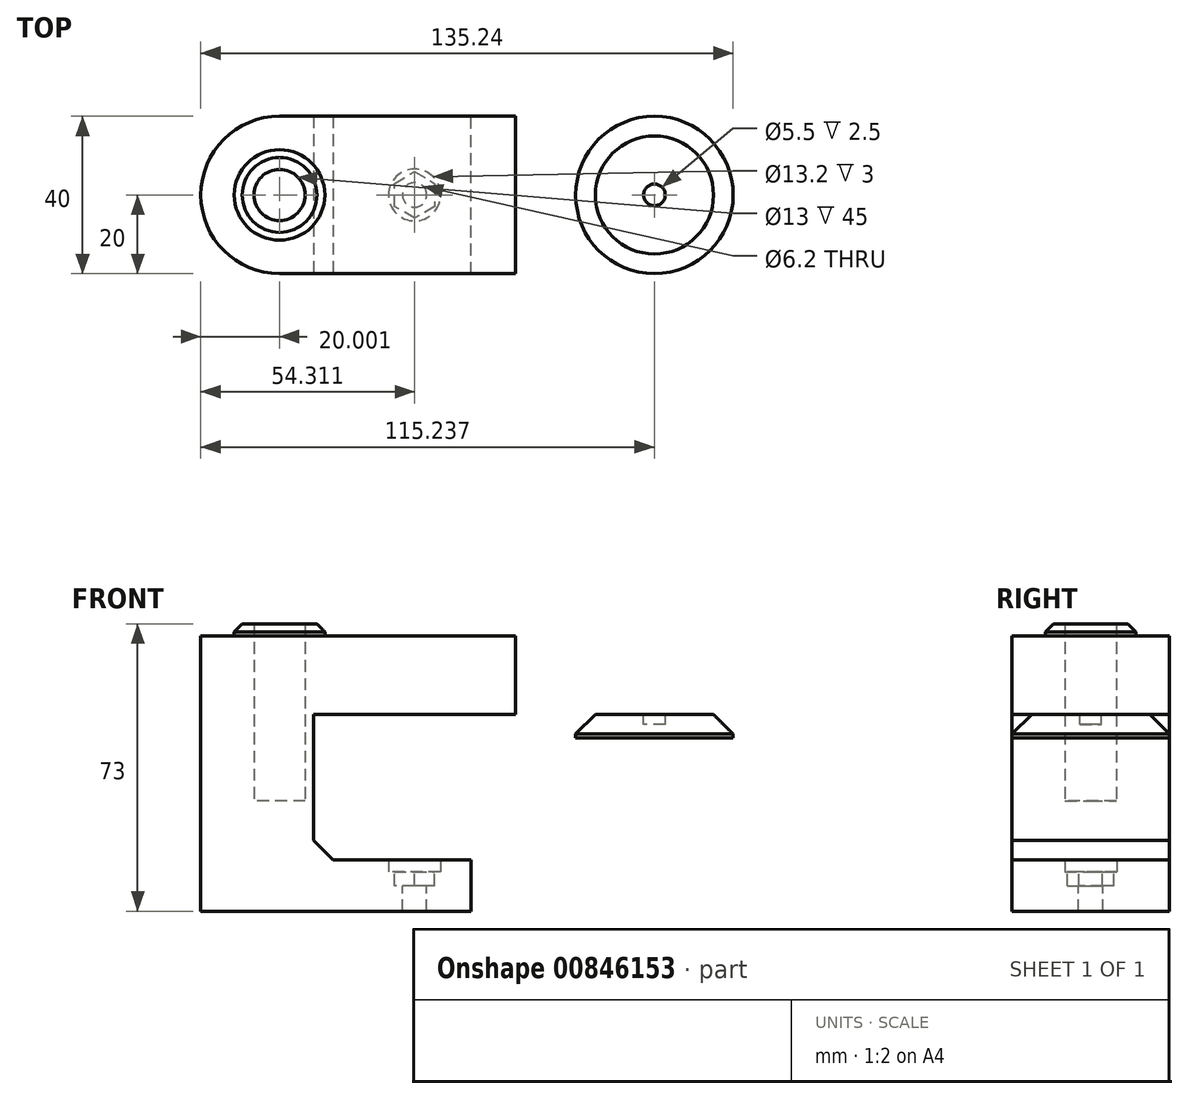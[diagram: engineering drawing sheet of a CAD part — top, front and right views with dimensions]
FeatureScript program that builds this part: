
annotation { "Feature Type Name" : "Feature", "Feature Type Description" : "" }
export const myFeature = defineFeature(function(context is Context, id is Id, definition is map)
    precondition{}
    {
        {
            var Q0;
            Q0=qCreatedBy(makeId("Top.planeOp"),FACE);
            var sketch = newSketch(context, id + "F0", { "sketchPlane" : qUnion([Q0])});
            skCircle(sketch, "E0", {"center": v(-23.62, 0) * mm, "radius": 6.5 * mm});
            skLineSegment(sketch, "E1", {"start": v(-23.62, 20) * mm, "end": v(36.38, 20) * mm});
            skLineSegment(sketch, "E2", {"start": v(36.38, 20) * mm, "end": v(36.38, -20) * mm});
            skLineSegment(sketch, "E3", {"start": v(36.38, -20) * mm, "end": v(-23.62, -20) * mm});
            skLineSegment(sketch, "E4", {"start": v(-69.54, 0) * mm, "end": v(66.59, 0) * mm, "construction": true});
            skLineSegment(sketch, "E5", {"start": v(-23.62, 57.59) * mm, "end": v(-23.62, -47.6) * mm, "construction": true});
            skPoint(sketch, "E6", {"position": v(36.38, 0) * mm});
            skCircle(sketch, "E7", {"center": v(-23.62, 0) * mm, "radius": 20 * mm});
            skPoint(sketch, "E8", {"position": v(-43.62, 0) * mm});
            skPoint(sketch, "E9", {"position": v(-23.62, 20) * mm});
            skPoint(sketch, "E10", {"position": v(-23.62, -20) * mm});
            skSolve(sketch);
        }
        {
            var Q0;
            {var subQ0=sQuery(id+"F0.wireOp",EDGE,"E1");Q0=makeQuery(id+"F0.imprint","IMPRINT",FACE,{"disambiguationData":[TD([[makeQuery(id+"F0.imprint","IMPRINT",EDGE,{"derivedFrom":subQ0}),-1.0]])]});}
            var Q1;
            Q1=makeQuery(id+"F0.imprint","IMPRINT",FACE,{"disambiguationData":[TD([[makeQuery(id+"F0.imprint","IMPRINT",EDGE,{"derivedFrom":sQuery(id+"F0.wireOp",EDGE,"E0")}),-1.0]])]});
            extrude(context, id + "F1", {"entities" : qUnion([Q0, Q1]), "depth" : 20 * mm, "offsetDistance" : 25 * mm});
        }
        {
            var Q0;
            Q0=qCreatedBy(makeId("Top.planeOp"),FACE);
            var sketch = newSketch(context, id + "F2", { "sketchPlane" : qUnion([Q0])});
            skLineSegment(sketch, "E11", {"start": v(-15, 20) * mm, "end": v(-15, -20) * mm});
            skPoint(sketch, "E12", {"position": v(-15, 0) * mm});
            skLineSegment(sketch, "E13", {"start": v(-15, 20) * mm, "end": v(-23.62, 20) * mm});
            skLineSegment(sketch, "E14.MirrorCS", {"start": v(-15, -20) * mm, "end": v(-23.62, -20) * mm});
            skArc(sketch, "E15", {"start": v(-23.62, 20) * mm, "mid": v(-43.62, 0) * mm, "end": v(-23.62, -20) * mm});
            skSolve(sketch);
        }
        {
            var Q0;
            Q0 = qSketchRegion(id + "F2", true);
            extrude(context, id + "F3", {"entities" : qUnion([Q0]), "operationType" : NewBodyOperationType.ADD, "oppositeDirection" : true, "depth" : 50 * mm, "offsetDistance" : 25 * mm});
        }
        {
            var Q0;
            Q0=makeQuery(id+"F0.imprint","IMPRINT",FACE,{"disambiguationData":[TD([[makeQuery(id+"F0.imprint","IMPRINT",EDGE,{"derivedFrom":sQuery(id+"F0.wireOp",EDGE,"E0")}),1.0]])]});
            extrude(context, id + "F4", {"entities" : qUnion([Q0]), "operationType" : NewBodyOperationType.REMOVE, "oppositeDirection" : true, "depth" : 22 * mm, "offsetDistance" : 25 * mm});
        }
        {
            var Q0;
            Q0=makeQuery(id+"F3.opExtrude","CAP_FACE",FACE,{"disambiguationData":[OSD([sQuery(id+"F2.wireOp",EDGE,"E11"),sQuery(id+"F2.wireOp",EDGE,"E13"),sQuery(id+"F2.wireOp",EDGE,"E14.MirrorCS"),sQuery(id+"F2.wireOp",EDGE,"E15")])],"isStart":false});
            var sketch = newSketch(context, id + "F5", { "sketchPlane" : qUnion([Q0])});
            skLineSegment(sketch, "E16.bottom", {"start": v(25, 20) * mm, "end": v(-15, 20) * mm});
            skLineSegment(sketch, "E16.top", {"start": v(25, -20) * mm, "end": v(-15, -20) * mm});
            skLineSegment(sketch, "E16.left", {"start": v(25, 20) * mm, "end": v(25, -20) * mm});
            skLineSegment(sketch, "E16.right", {"start": v(-15, 20) * mm, "end": v(-15, -20) * mm});
            skPoint(sketch, "E16.middle", {"position": v(5, 0) * mm});
            skSolve(sketch);
        }
        {
            var Q0;
            Q0=makeQuery(id+"F5.imprint","IMPRINT",FACE,{"disambiguationData":[TD([[makeQuery(id+"F5.imprint","IMPRINT",EDGE,{"derivedFrom":sQuery(id+"F5.wireOp",EDGE,"E16.bottom")}),1.0]])]});
            extrude(context, id + "F6", {"entities" : qUnion([Q0]), "operationType" : NewBodyOperationType.ADD, "oppositeDirection" : true, "depth" : 10 * mm, "offsetDistance" : 25 * mm});
        }
        {
            var Q0;
            Q0=makeQuery(id+"F1.opExtrude","CAP_FACE",FACE,{"disambiguationData":[OSD([sQuery(id+"F0.wireOp",EDGE,"E0"),sQuery(id+"F0.wireOp",EDGE,"E1"),sQuery(id+"F0.wireOp",EDGE,"E2"),sQuery(id+"F0.wireOp",EDGE,"E3"),sQuery(id+"F0.wireOp",EDGE,"E7")])],"isStart":false});
            var sketch = newSketch(context, id + "F7", { "sketchPlane" : qUnion([Q0])});
            skCircle(sketch, "E17", {"center": v(-23.62, 0) * mm, "radius": 11.5 * mm});
            skSolve(sketch);
        }
        {
            var Q0;
            Q0=makeQuery(id+"F7.imprint","IMPRINT",FACE,{"disambiguationData":[TD([[makeQuery(id+"F7.imprint","IMPRINT",EDGE,{"derivedFrom":sQuery(id+"F7.wireOp",EDGE,"E17")}),1.0]])]});
            extrude(context, id + "F8", {"entities" : qUnion([Q0]), "operationType" : NewBodyOperationType.ADD, "depth" : 3 * mm, "offsetDistance" : 25 * mm});
        }
        {
            var Q0;
            Q0=makeQuery(id+"F8.opExtrude","CAP_EDGE",EDGE,{"disambiguationData":[OSD([sQuery(id+"F7.wireOp",EDGE,"E17")])],"isStart":false});
            chamfer(context, id + "F9", {"entities" : qUnion([Q0]), "width" : 2 * mm, "tangentPropagation" : true});
        }
        {
            var Q0;
            Q0=makeQuery(id+"F6.opExtrude","CAP_FACE",FACE,{"disambiguationData":[OSD([sQuery(id+"F5.wireOp",EDGE,"E16.bottom"),sQuery(id+"F5.wireOp",EDGE,"E16.top"),sQuery(id+"F5.wireOp",EDGE,"E16.left"),sQuery(id+"F5.wireOp",EDGE,"E16.right")])],"isStart":false});
            var sketch = newSketch(context, id + "F10", { "sketchPlane" : qUnion([Q0])});
            skPoint(sketch, "E18", {"position": v(-15, -20) * mm});
            skLineSegment(sketch, "E19", {"start": v(-15, -20) * mm, "end": v(-15, 20) * mm, "construction": true});
            skLineSegment(sketch, "E20", {"start": v(-15, 0) * mm, "end": v(36.38, 0) * mm, "construction": true});
            skCircle(sketch, "E21", {"center": v(10.7, 0) * mm, "radius": 6.6 * mm});
            skCircle(sketch, "E22.cCircle", {"center": v(10.7, 0) * mm, "radius": 5.1 * mm, "construction": true});
            skLineSegment(sketch, "E22.0", {"start": v(5.58, -2.95) * mm, "end": v(5.58, 2.95) * mm});
            skLineSegment(sketch, "E22.1", {"start": v(5.58, 2.95) * mm, "end": v(10.7, 5.9) * mm});
            skLineSegment(sketch, "E22.2", {"start": v(10.7, 5.9) * mm, "end": v(15.8, 2.95) * mm});
            skLineSegment(sketch, "E22.3", {"start": v(15.8, 2.95) * mm, "end": v(15.8, -2.95) * mm});
            skLineSegment(sketch, "E22.4", {"start": v(15.8, -2.95) * mm, "end": v(10.7, -5.9) * mm});
            skLineSegment(sketch, "E22.5", {"start": v(10.7, -5.9) * mm, "end": v(5.58, -2.95) * mm});
            skSolve(sketch);
        }
        {
            var Q0;
            Q0=makeQuery(id+"F10.imprint","IMPRINT",FACE,{"disambiguationData":[TD([[makeQuery(id+"F10.imprint","IMPRINT",EDGE,{"derivedFrom":sQuery(id+"F10.wireOp",EDGE,"E22.0")}),-1.0]])]});
            extrude(context, id + "F11", {"entities" : qUnion([Q0]), "operationType" : NewBodyOperationType.REMOVE, "oppositeDirection" : true, "depth" : 3.5 * mm, "offsetDistance" : 25 * mm});
        }
        {
            var Q0;
            Q0=makeQuery(id+"F10.imprint","IMPRINT",FACE,{"disambiguationData":[TD([[makeQuery(id+"F10.imprint","IMPRINT",EDGE,{"derivedFrom":sQuery(id+"F10.wireOp",EDGE,"E22.0")}),-1.0]])]});
            var Q1;
            Q1=makeQuery(id+"F10.imprint","IMPRINT",FACE,{"disambiguationData":[TD([[makeQuery(id+"F10.imprint","IMPRINT",EDGE,{"derivedFrom":sQuery(id+"F10.wireOp",EDGE,"E21")}),1.0]])]});
            var Q2;
            Q2=makeQuery(id+"F10.imprint","IMPRINT",FACE,{"disambiguationData":[TD([[makeQuery(id+"F10.imprint","IMPRINT",EDGE,{"derivedFrom":sQuery(id+"F10.wireOp",EDGE,"E21")}),-1.0]])]});
            extrude(context, id + "F12", {"entities" : qUnion([Q0, Q1, Q2]), "operationType" : NewBodyOperationType.ADD, "depth" : 3 * mm, "offsetDistance" : 25 * mm});
        }
        {
            var Q0;
            Q0=makeQuery(id+"F10.imprint","IMPRINT",FACE,{"disambiguationData":[TD([[makeQuery(id+"F10.imprint","IMPRINT",EDGE,{"derivedFrom":sQuery(id+"F10.wireOp",EDGE,"E21")}),1.0]])]});
            var Q1;
            Q1=makeQuery(id+"F10.imprint","IMPRINT",FACE,{"disambiguationData":[TD([[makeQuery(id+"F10.imprint","IMPRINT",EDGE,{"derivedFrom":sQuery(id+"F10.wireOp",EDGE,"E22.0")}),-1.0]])]});
            extrude(context, id + "F13", {"entities" : qUnion([Q0, Q1]), "operationType" : NewBodyOperationType.REMOVE, "depth" : 3 * mm, "offsetDistance" : 25 * mm});
        }
        {
            var Q0;
            Q0=sQuery(id+"F10.wireOp",VERTEX,"E21.center");
            var Q1;
            Q1=makeQuery(id+"F1.opExtrude","SWEPT_BODY",BODY,{"disambiguationData":[OSD([sQuery(id+"F0.wireOp",EDGE,"E0"),sQuery(id+"F0.wireOp",EDGE,"E1"),sQuery(id+"F0.wireOp",EDGE,"E2"),sQuery(id+"F0.wireOp",EDGE,"E3"),sQuery(id+"F0.wireOp",EDGE,"E7")])]});
            hole(context, id + "F14", {"style" : HoleStyle.SIMPLE, "endStyle" : HoleEndStyle.THROUGH, "holeDiameter" : 6.2 * mm, "majorDiameter" : 5 * mm, "isTappedThrough" : true, "tappedDepth" : 12 * mm, "tapClearance" : 3, "locations" : qUnion([Q0]), "scope" : qUnion([Q1])});
        }
        {
            var Q0;
            Q0=qCreatedBy(makeId("Top.planeOp"),FACE);
            var sketch = newSketch(context, id + "F15", { "sketchPlane" : qUnion([Q0])});
            skCircle(sketch, "E23", {"center": v(71.62, 0) * mm, "radius": 20 * mm});
            skCircle(sketch, "E24", {"center": v(71.62, 0) * mm, "radius": 2.75 * mm});
            skSolve(sketch);
        }
        {
            var Q0;
            Q0=makeQuery(id+"F15.imprint","IMPRINT",FACE,{"disambiguationData":[TD([[makeQuery(id+"F15.imprint","IMPRINT",EDGE,{"derivedFrom":sQuery(id+"F15.wireOp",EDGE,"E23")}),1.0]])]});
            var Q1;
            Q1=makeQuery(id+"F15.imprint","IMPRINT",FACE,{"disambiguationData":[TD([[makeQuery(id+"F15.imprint","IMPRINT",EDGE,{"derivedFrom":sQuery(id+"F15.wireOp",EDGE,"E24")}),1.0]])]});
            extrude(context, id + "F16", {"entities" : qUnion([Q0, Q1]), "depth" : 6 * mm, "offsetDistance" : 25 * mm});
        }
        {
            var Q0;
            Q0=makeQuery(id+"F16.opExtrude","CAP_EDGE",EDGE,{"disambiguationData":[OSD([sQuery(id+"F15.wireOp",EDGE,"E23")])],"isStart":true});
            chamfer(context, id + "F17", {"entities" : qUnion([Q0]), "width" : 5 * mm, "tangentPropagation" : true});
        }
        {
            var Q0;
            Q0=makeQuery(id+"F15.imprint","IMPRINT",FACE,{"disambiguationData":[TD([[makeQuery(id+"F15.imprint","IMPRINT",EDGE,{"derivedFrom":sQuery(id+"F15.wireOp",EDGE,"E24")}),1.0]])]});
            extrude(context, id + "F18", {"entities" : qUnion([Q0]), "operationType" : NewBodyOperationType.REMOVE, "depth" : 2.5 * mm, "offsetDistance" : 25 * mm});
        }
        {
            var Q0;
            Q0=makeQuery(id+"F16.opExtrude","SWEPT_BODY",BODY,{"disambiguationData":[OSD([sQuery(id+"F15.wireOp",EDGE,"E23")])]});
            var Q1;
            Q1=sQuery(id+"F0.wireOp",EDGE,"E4");
            transform(context, id + "F19", {"entities" : qUnion([Q0]), "transformType" : TransformType.ROTATION, "transformAxis" : qUnion([Q1]), "angle" : 180 * degree, "makeCopy" : false});
        }
        {
            var Q0;
            {var subQ0=sQuery(id+"F5.wireOp",EDGE,"E16.bottom");Q0=makeQuery(id+"F12.boolean.opBoolean","MERGE",FACE,{"derivedFrom":[makeQuery(id+"F6.boolean.opBoolean","MERGE",FACE,{"derivedFrom":[makeQuery(id+"F3.boolean.opBoolean","MERGE",FACE,{"derivedFrom":[makeQuery(id+"F1.opExtrude","SWEPT_FACE",FACE,{"disambiguationData":[OSD([sQuery(id+"F0.wireOp",EDGE,"E3")])]}),makeQuery(id+"F3.opExtrude","SWEPT_FACE",FACE,{"disambiguationData":[OSD([sQuery(id+"F2.wireOp",EDGE,"E14.MirrorCS")])]})]}),makeQuery(id+"F6.opExtrude","SWEPT_FACE",FACE,{"disambiguationData":[OSD([subQ0])]})]}),makeQuery(id+"F12.opExtrude","SWEPT_FACE",FACE,{"disambiguationData":[OSD([subQ0])]})]});}
            var sketch = newSketch(context, id + "F20", { "sketchPlane" : qUnion([Q0])});
            skLineSegment(sketch, "E25", {"start": v(-15, -37) * mm, "end": v(-10, -37) * mm});
            skLineSegment(sketch, "E26", {"start": v(-10, -37) * mm, "end": v(-15, -32) * mm});
            skLineSegment(sketch, "E27", {"start": v(-15, -32) * mm, "end": v(-15, -37) * mm});
            skSolve(sketch);
        }
        {
            var Q0;
            Q0=makeQuery(id+"F20.imprint","IMPRINT",FACE,{"disambiguationData":[TD([[makeQuery(id+"F20.imprint","IMPRINT",EDGE,{"derivedFrom":sQuery(id+"F20.wireOp",EDGE,"E25")}),-1.0]])]});
            extrude(context, id + "F21", {"entities" : qUnion([Q0]), "operationType" : NewBodyOperationType.ADD, "oppositeDirection" : true, "depth" : 40 * mm, "offsetDistance" : 25 * mm});
        }
    });
